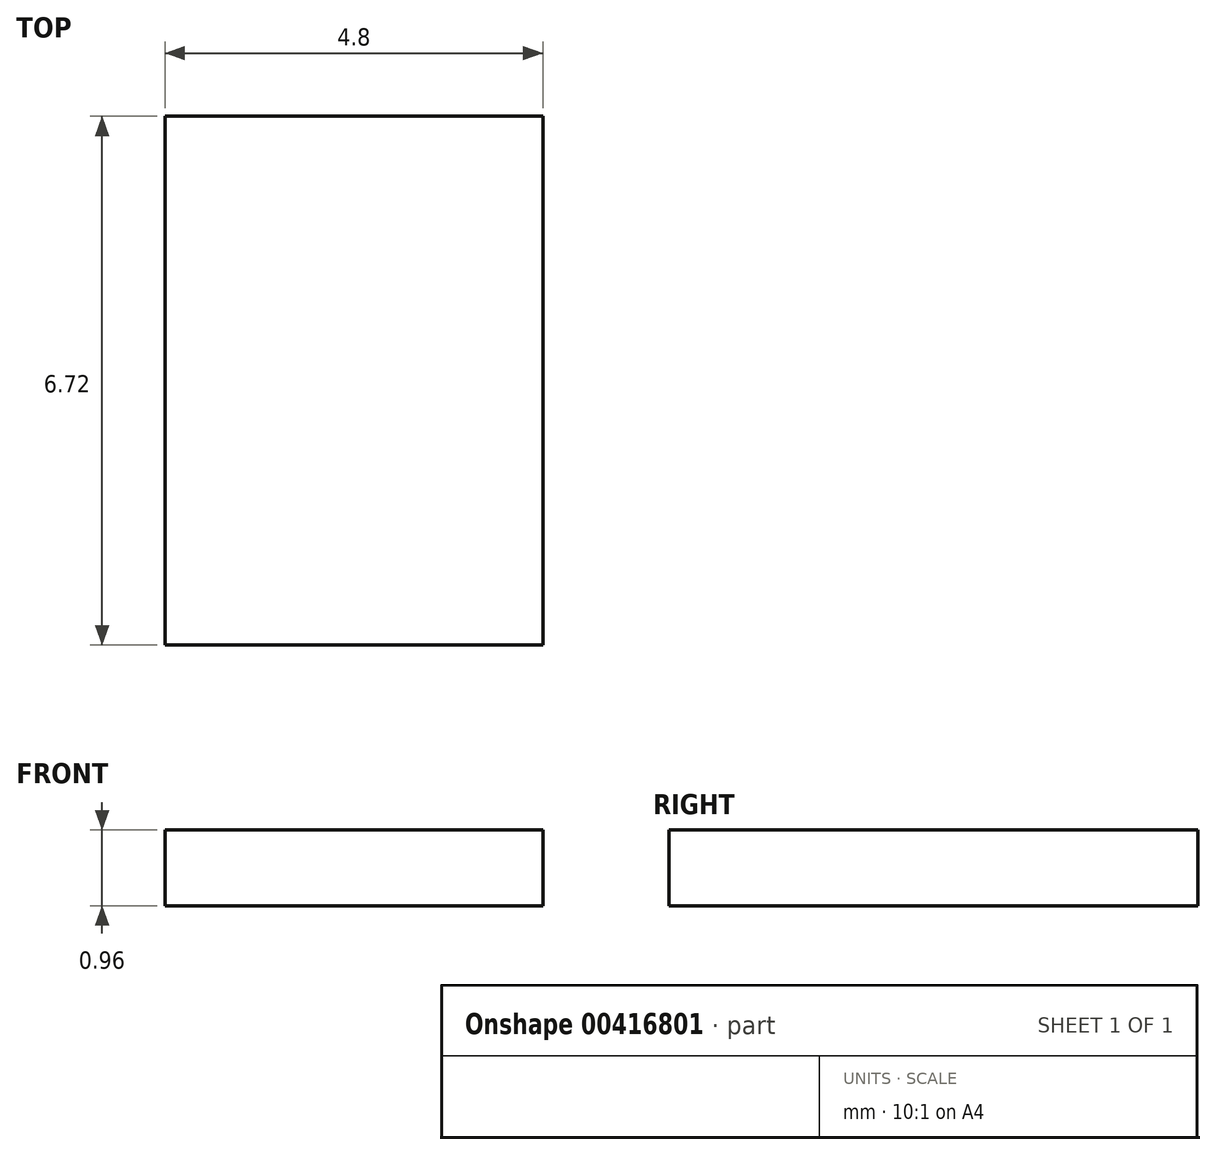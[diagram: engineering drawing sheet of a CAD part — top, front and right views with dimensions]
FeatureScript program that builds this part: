
annotation { "Feature Type Name" : "Feature", "Feature Type Description" : "" }
export const myFeature = defineFeature(function(context is Context, id is Id, definition is map)
    precondition{}
    {
        {
            var Q0;
            Q0=qCreatedBy(makeId("Top.planeOp"),FACE);
            var sketch = newSketch(context, id + "F0", { "sketchPlane" : qUnion([Q0])});
            skLineSegment(sketch, "E0.bottom", {"start": v(0, 0) * mm, "end": v(4.8, 0) * mm});
            skLineSegment(sketch, "E0.top", {"start": v(0, 6.72) * mm, "end": v(4.8, 6.72) * mm});
            skLineSegment(sketch, "E0.left", {"start": v(0, 0) * mm, "end": v(0, 6.72) * mm});
            skLineSegment(sketch, "E0.right", {"start": v(4.8, 0) * mm, "end": v(4.8, 6.72) * mm});
            skSolve(sketch);
        }
        {
            var Q0;
            Q0 = qSketchRegion(id + "F0", true);
            extrude(context, id + "F1", {"entities" : qUnion([Q0]), "depth" : .96 * mm, "offsetDistance" : 25.4 * mm});
        }
    });
